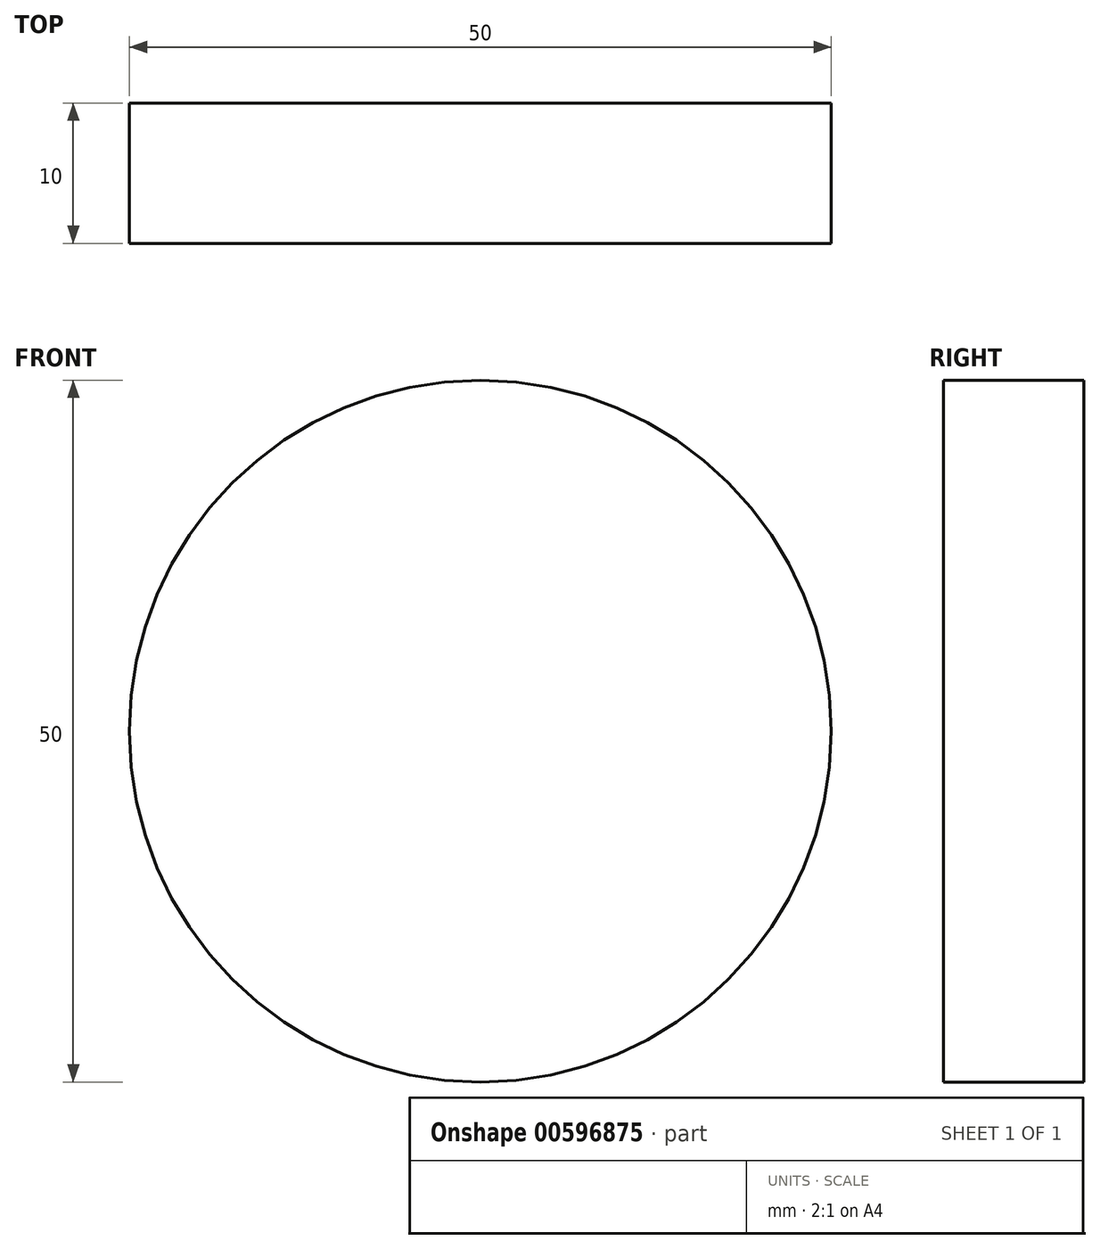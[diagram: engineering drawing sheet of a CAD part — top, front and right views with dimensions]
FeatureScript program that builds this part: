
annotation { "Feature Type Name" : "Feature", "Feature Type Description" : "" }
export const myFeature = defineFeature(function(context is Context, id is Id, definition is map)
    precondition{}
    {
        {
            var Q0;
            Q0=qCreatedBy(makeId("Front.planeOp"),FACE);
            var sketch = newSketch(context, id + "F0", { "sketchPlane" : qUnion([Q0])});
            skCircle(sketch, "E0", {"center": v(0, 0) * mm, "radius": 25 * mm});
            skSolve(sketch);
        }
        {
            var Q0;
            Q0=makeQuery(id+"F0.imprint","IMPRINT",FACE,{"disambiguationData":[TD([[makeQuery(id+"F0.imprint","IMPRINT",EDGE,{"derivedFrom":sQuery(id+"F0.wireOp",EDGE,"E0")}),1.0]])]});
            extrude(context, id + "F1", {"entities" : qUnion([Q0]), "depth" : 10 * mm, "offsetDistance" : 25 * mm});
        }
    });
